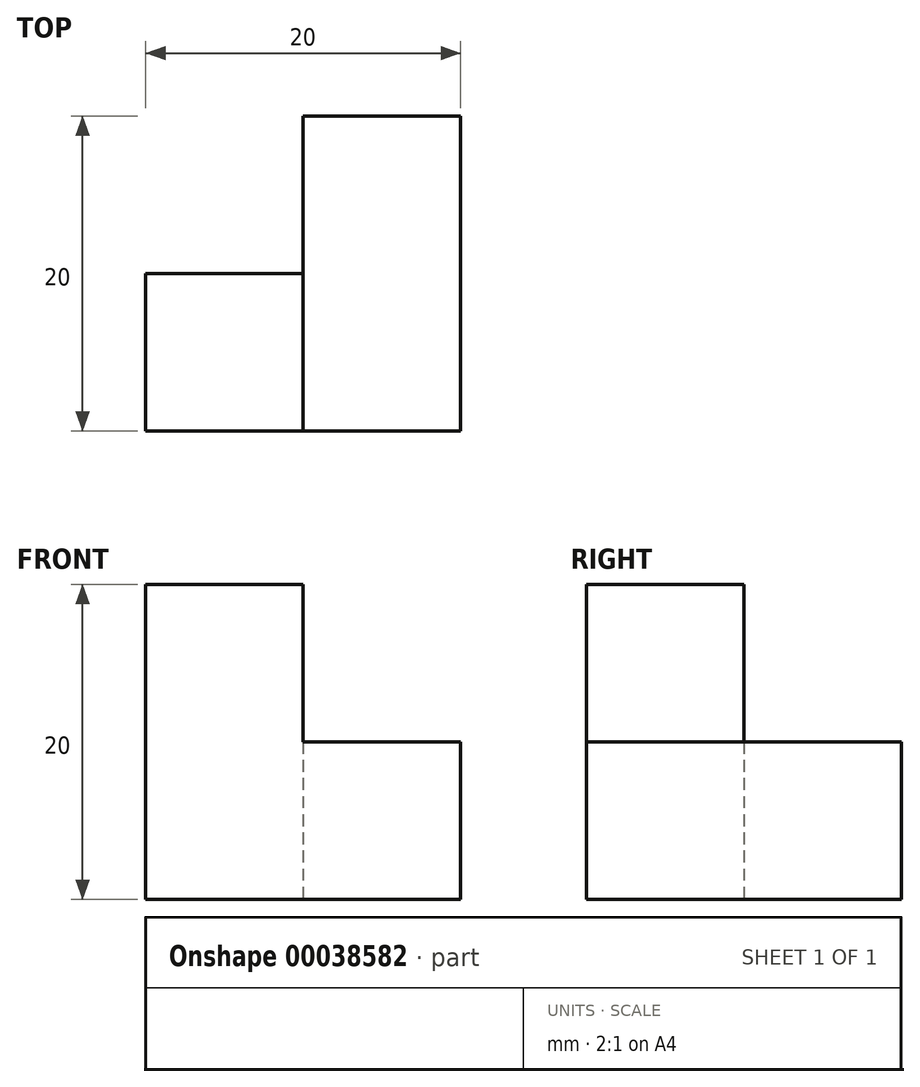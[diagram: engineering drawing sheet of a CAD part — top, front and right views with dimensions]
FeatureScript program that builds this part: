
annotation { "Feature Type Name" : "Feature", "Feature Type Description" : "" }
export const myFeature = defineFeature(function(context is Context, id is Id, definition is map)
    precondition{}
    {
        {
            var Q0;
            Q0=qCreatedBy(makeId("Top.planeOp"),FACE);
            var sketch = newSketch(context, id + "F0", { "sketchPlane" : qUnion([Q0])});
            skLineSegment(sketch, "E0.bottom", {"start": v(0, 0) * mm, "end": v(10, 0) * mm});
            skLineSegment(sketch, "E0.top", {"start": v(0, 10) * mm, "end": v(10, 10) * mm});
            skLineSegment(sketch, "E0.left", {"start": v(0, 0) * mm, "end": v(0, 10) * mm});
            skLineSegment(sketch, "E0.right", {"start": v(10, 0) * mm, "end": v(10, 10) * mm});
            skSolve(sketch);
        }
        {
            var Q0;
            Q0=makeQuery(id+"F0.imprint","IMPRINT",FACE,{"disambiguationData":[TD([[makeQuery(id+"F0.imprint","IMPRINT",EDGE,{"derivedFrom":sQuery(id+"F0.wireOp",EDGE,"E0.bottom")}),1.0]])]});
            extrude(context, id + "F1", {"entities" : qUnion([Q0]), "depth" : 20 * mm});
        }
        {
            var Q0;
            Q0=makeQuery(id+"F1.opExtrude","SWEPT_FACE",FACE,{"disambiguationData":[OSD([sQuery(id+"F0.wireOp",EDGE,"E0.right")])]});
            var sketch = newSketch(context, id + "F2", { "sketchPlane" : qUnion([Q0])});
            skLineSegment(sketch, "E1.bottom", {"start": v(0, 0) * mm, "end": v(10, 0) * mm});
            skLineSegment(sketch, "E1.top", {"start": v(0, 10) * mm, "end": v(10, 10) * mm});
            skLineSegment(sketch, "E1.left", {"start": v(0, 0) * mm, "end": v(0, 10) * mm});
            skLineSegment(sketch, "E1.right", {"start": v(10, 0) * mm, "end": v(10, 10) * mm});
            skSolve(sketch);
        }
        {
            var Q0;
            Q0 = qSketchRegion(id + "F2", true);
            extrude(context, id + "F3", {"entities" : qUnion([Q0]), "operationType" : NewBodyOperationType.ADD, "depth" : 10 * mm});
        }
        {
            var Q0;
            Q0=makeQuery(id+"F3.boolean.opBoolean","MERGE",FACE,{"derivedFrom":[makeQuery(id+"F1.opExtrude","SWEPT_FACE",FACE,{"disambiguationData":[OSD([sQuery(id+"F0.wireOp",EDGE,"E0.top")])]}),makeQuery(id+"F3.opExtrude","SWEPT_FACE",FACE,{"disambiguationData":[OSD([sQuery(id+"F2.wireOp",EDGE,"E1.right")])]})]});
            var sketch = newSketch(context, id + "F4", { "sketchPlane" : qUnion([Q0])});
            skLineSegment(sketch, "E2.bottom", {"start": v(-20, 10) * mm, "end": v(-10, 10) * mm});
            skLineSegment(sketch, "E2.top", {"start": v(-20, 0) * mm, "end": v(-10, 0) * mm});
            skLineSegment(sketch, "E2.left", {"start": v(-20, 10) * mm, "end": v(-20, 0) * mm});
            skLineSegment(sketch, "E2.right", {"start": v(-10, 10) * mm, "end": v(-10, 0) * mm});
            skSolve(sketch);
        }
        {
            var Q0;
            Q0 = qSketchRegion(id + "F4", true);
            extrude(context, id + "F5", {"entities" : qUnion([Q0]), "operationType" : NewBodyOperationType.ADD, "depth" : 10 * mm});
        }
    });
